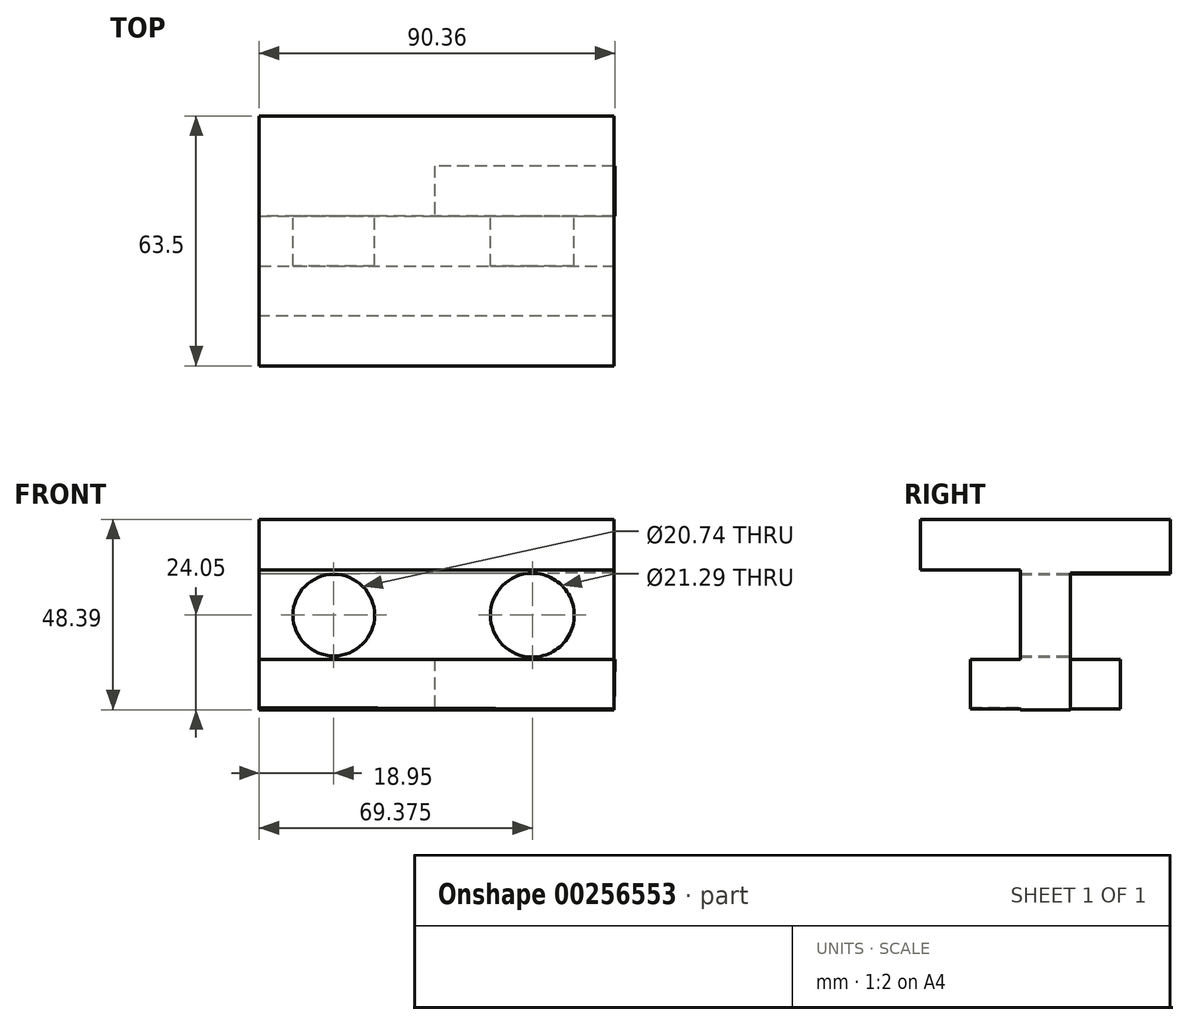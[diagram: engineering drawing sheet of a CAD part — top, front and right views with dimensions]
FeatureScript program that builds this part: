
annotation { "Feature Type Name" : "Feature", "Feature Type Description" : "" }
export const myFeature = defineFeature(function(context is Context, id is Id, definition is map)
    precondition{}
    {
        {
            var Q0;
            Q0=qCreatedBy(makeId("Front.planeOp"),FACE);
            var sketch = newSketch(context, id + "F0", { "sketchPlane" : qUnion([Q0])});
            skLineSegment(sketch, "E0.bottom", {"start": v(-44.6, 24.34) * mm, "end": v(45.47, 24.34) * mm});
            skLineSegment(sketch, "E0.top", {"start": v(-44.6, -24.05) * mm, "end": v(45.47, -24.05) * mm});
            skLineSegment(sketch, "E0.left", {"start": v(-44.6, 24.34) * mm, "end": v(-44.6, -24.05) * mm});
            skLineSegment(sketch, "E0.right", {"start": v(45.47, 24.34) * mm, "end": v(45.47, -24.05) * mm});
            skCircle(sketch, "E1", {"center": v(-25.65, 0) * mm, "radius": 10.37 * mm});
            skCircle(sketch, "E2", {"center": v(24.78, 0) * mm, "radius": 10.64 * mm});
            skSolve(sketch);
        }
        {
            var Q0;
            Q0=makeQuery(id+"F0.imprint","IMPRINT",FACE,{"disambiguationData":[TD([[makeQuery(id+"F0.imprint","IMPRINT",EDGE,{"derivedFrom":sQuery(id+"F0.wireOp",EDGE,"E0.bottom")}),-1.0]])]});
            extrude(context, id + "F1", {"entities" : qUnion([Q0]), "depth" : 12.7 * mm});
        }
        {
            var Q0;
            Q0=makeQuery(id+"F1.opExtrude","CAP_FACE",FACE,{"disambiguationData":[OSD([sQuery(id+"F0.wireOp",EDGE,"E0.bottom"),sQuery(id+"F0.wireOp",EDGE,"E0.top"),sQuery(id+"F0.wireOp",EDGE,"E0.left"),sQuery(id+"F0.wireOp",EDGE,"E0.right"),sQuery(id+"F0.wireOp",EDGE,"E1"),sQuery(id+"F0.wireOp",EDGE,"E2")])],"isStart":true});
            var sketch = newSketch(context, id + "F2", { "sketchPlane" : qUnion([Q0])});
            skLineSegment(sketch, "E3", {"start": v(-45.47, 24.34) * mm, "end": v(-45.47, 10.7) * mm});
            skLineSegment(sketch, "E4", {"start": v(-45.47, 10.7) * mm, "end": v(44.6, 10.46) * mm});
            skLineSegment(sketch, "E5", {"start": v(44.6, 10.46) * mm, "end": v(44.6, 24.34) * mm});
            skLineSegment(sketch, "E6", {"start": v(44.6, 24.34) * mm, "end": v(-45.47, 24.34) * mm});
            skSolve(sketch);
        }
        {
            var Q0;
            {var subQ3=sQuery(id+"F2.wireOp",EDGE,"E3");Q0=makeQuery(id+"F2.imprint","IMPRINT",FACE,{"disambiguationData":[TD([[makeQuery(id+"F2.imprint","IMPRINT",EDGE,{"derivedFrom":subQ3}),1.0]])]});}
            extrude(context, id + "F3", {"entities" : qUnion([Q0]), "operationType" : NewBodyOperationType.ADD, "depth" : 25.4 * mm});
        }
        {
            var Q0;
            Q0=makeQuery(id+"F1.opExtrude","CAP_FACE",FACE,{"disambiguationData":[OSD([sQuery(id+"F0.wireOp",EDGE,"E0.bottom"),sQuery(id+"F0.wireOp",EDGE,"E0.top"),sQuery(id+"F0.wireOp",EDGE,"E0.left"),sQuery(id+"F0.wireOp",EDGE,"E0.right"),sQuery(id+"F0.wireOp",EDGE,"E1"),sQuery(id+"F0.wireOp",EDGE,"E2")])],"isStart":false});
            var sketch = newSketch(context, id + "F4", { "sketchPlane" : qUnion([Q0])});
            skLineSegment(sketch, "E7", {"start": v(-44.6, 11.51) * mm, "end": v(45.47, 11.51) * mm});
            skLineSegment(sketch, "E8", {"start": v(45.47, 11.51) * mm, "end": v(45.47, 24.34) * mm});
            skLineSegment(sketch, "E9", {"start": v(45.47, 24.34) * mm, "end": v(-44.6, 24.34) * mm});
            skLineSegment(sketch, "E10", {"start": v(-44.6, 24.34) * mm, "end": v(-44.6, 11.51) * mm});
            skSolve(sketch);
        }
        {
            var Q0;
            Q0=makeQuery(id+"F4.imprint","IMPRINT",FACE,{"disambiguationData":[TD([[makeQuery(id+"F4.imprint","IMPRINT",EDGE,{"derivedFrom":sQuery(id+"F4.wireOp",EDGE,"E7")}),1.0]])]});
            extrude(context, id + "F5", {"entities" : qUnion([Q0]), "operationType" : NewBodyOperationType.ADD, "depth" : 25.4 * mm});
        }
        {
            var Q0;
            Q0=qCreatedBy(makeId("Front.planeOp"),FACE);
            var sketch = newSketch(context, id + "F6", { "sketchPlane" : qUnion([Q0])});
            skLineSegment(sketch, "E11", {"start": v(45.47, -11.22) * mm, "end": v(-44.6, -11.22) * mm});
            skLineSegment(sketch, "E12", {"start": v(-44.6, -11.22) * mm, "end": v(-44.6, -23.46) * mm});
            skLineSegment(sketch, "E13", {"start": v(45.47, -11.22) * mm, "end": v(45.47, -23.76) * mm});
            skLineSegment(sketch, "E14", {"start": v(45.47, -23.76) * mm, "end": v(-44.6, -23.46) * mm});
            skSolve(sketch);
        }
        {
            var Q0;
            Q0=makeQuery(id+"F6.imprint","IMPRINT",FACE,{"disambiguationData":[TD([[makeQuery(id+"F6.imprint","IMPRINT",EDGE,{"derivedFrom":sQuery(id+"F6.wireOp",EDGE,"E11")}),1.0]])]});
            extrude(context, id + "F7", {"entities" : qUnion([Q0]), "operationType" : NewBodyOperationType.ADD, "depth" : 25.4 * mm});
        }
        {
            var Q0;
            Q0=qCreatedBy(makeId("Front.planeOp"),FACE);
            var sketch = newSketch(context, id + "F8", { "sketchPlane" : qUnion([Q0])});
            skLineSegment(sketch, "E15", {"start": v(45.76, -11.22) * mm, "end": v(0, -11.22) * mm});
            skLineSegment(sketch, "E16", {"start": v(0, -11.22) * mm, "end": v(0, -23.76) * mm});
            skLineSegment(sketch, "E17", {"start": v(0, -23.76) * mm, "end": v(45.47, -23.76) * mm});
            skLineSegment(sketch, "E18", {"start": v(45.47, -23.76) * mm, "end": v(45.76, -11.22) * mm});
            skSolve(sketch);
        }
        {
            var Q0;
            Q0=makeQuery(id+"F8.imprint","IMPRINT",FACE,{"disambiguationData":[TD([[makeQuery(id+"F8.imprint","IMPRINT",EDGE,{"derivedFrom":sQuery(id+"F8.wireOp",EDGE,"E15")}),1.0]])]});
            extrude(context, id + "F9", {"entities" : qUnion([Q0]), "operationType" : NewBodyOperationType.ADD, "oppositeDirection" : true, "depth" : 12.7 * mm});
        }
    });
